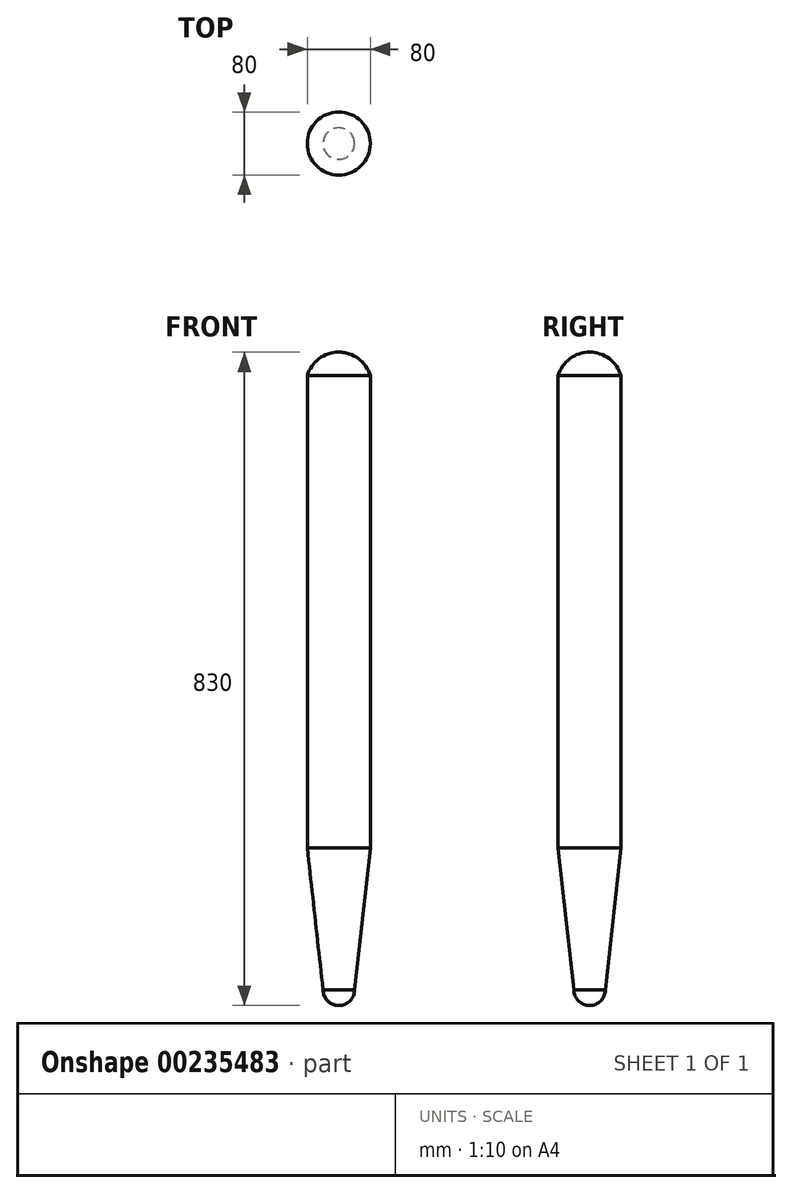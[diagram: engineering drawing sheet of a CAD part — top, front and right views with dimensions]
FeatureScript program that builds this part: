
annotation { "Feature Type Name" : "Feature", "Feature Type Description" : "" }
export const myFeature = defineFeature(function(context is Context, id is Id, definition is map)
    precondition{}
    {
        {
            var Q0;
            Q0=qCreatedBy(makeId("Front.planeOp"),FACE);
            var sketch = newSketch(context, id + "F0", { "sketchPlane" : qUnion([Q0])});
            skLineSegment(sketch, "E0.top", {"start": v(0, -300) * mm, "end": v(-40, -300) * mm, "construction": true});
            skLineSegment(sketch, "E0.left", {"start": v(40, 300) * mm, "end": v(40, -300) * mm});
            skLineSegment(sketch, "E0.right", {"start": v(-40, 300) * mm, "end": v(-40, -300) * mm});
            skPoint(sketch, "E0.middle", {"position": v(0, 0) * mm});
            skArc(sketch, "E1", {"start": v(-20, -480) * mm, "mid": v(0, -500) * mm, "end": v(20, -480) * mm});
            skPoint(sketch, "E1.centerSnap0", {"position": v(0, -300) * mm});
            skLineSegment(sketch, "E2", {"start": v(40, -300) * mm, "end": v(20, -480) * mm});
            skLineSegment(sketch, "E3", {"start": v(-40, -300) * mm, "end": v(-20, -480) * mm});
            skArc(sketch, "E4", {"start": v(40, 300) * mm, "mid": v(0, 330) * mm, "end": v(-40, 300) * mm});
            skLineSegment(sketch, "E5", {"start": v(-40, 300) * mm, "end": v(40, 300) * mm, "construction": true});
            skLineSegment(sketch, "E6", {"start": v(0, -722.05) * mm, "end": v(0, 542.45) * mm, "construction": true});
            skLineSegment(sketch, "E7", {"start": v(0, 388.51) * mm, "end": v(0, -550.68) * mm});
            skSolve(sketch);
        }
        {
            var Q0;
            {var subQ1=sQuery(id+"F0.wireOp",EDGE,"E0.left");Q0=makeQuery(id+"F0.imprint","IMPRINT",FACE,{"disambiguationData":[TD([[makeQuery(id+"F0.imprint","IMPRINT",EDGE,{"derivedFrom":subQ1}),-1.0]])]});}
            var Q1;
            Q1=sQuery(id+"F0.wireOp",EDGE,"E6");
            revolve(context, id + "F1", {"entities" : qUnion([Q0]), "axis" : qUnion([Q1]), "revolveType" : RevolveType.FULL});
        }
    });
